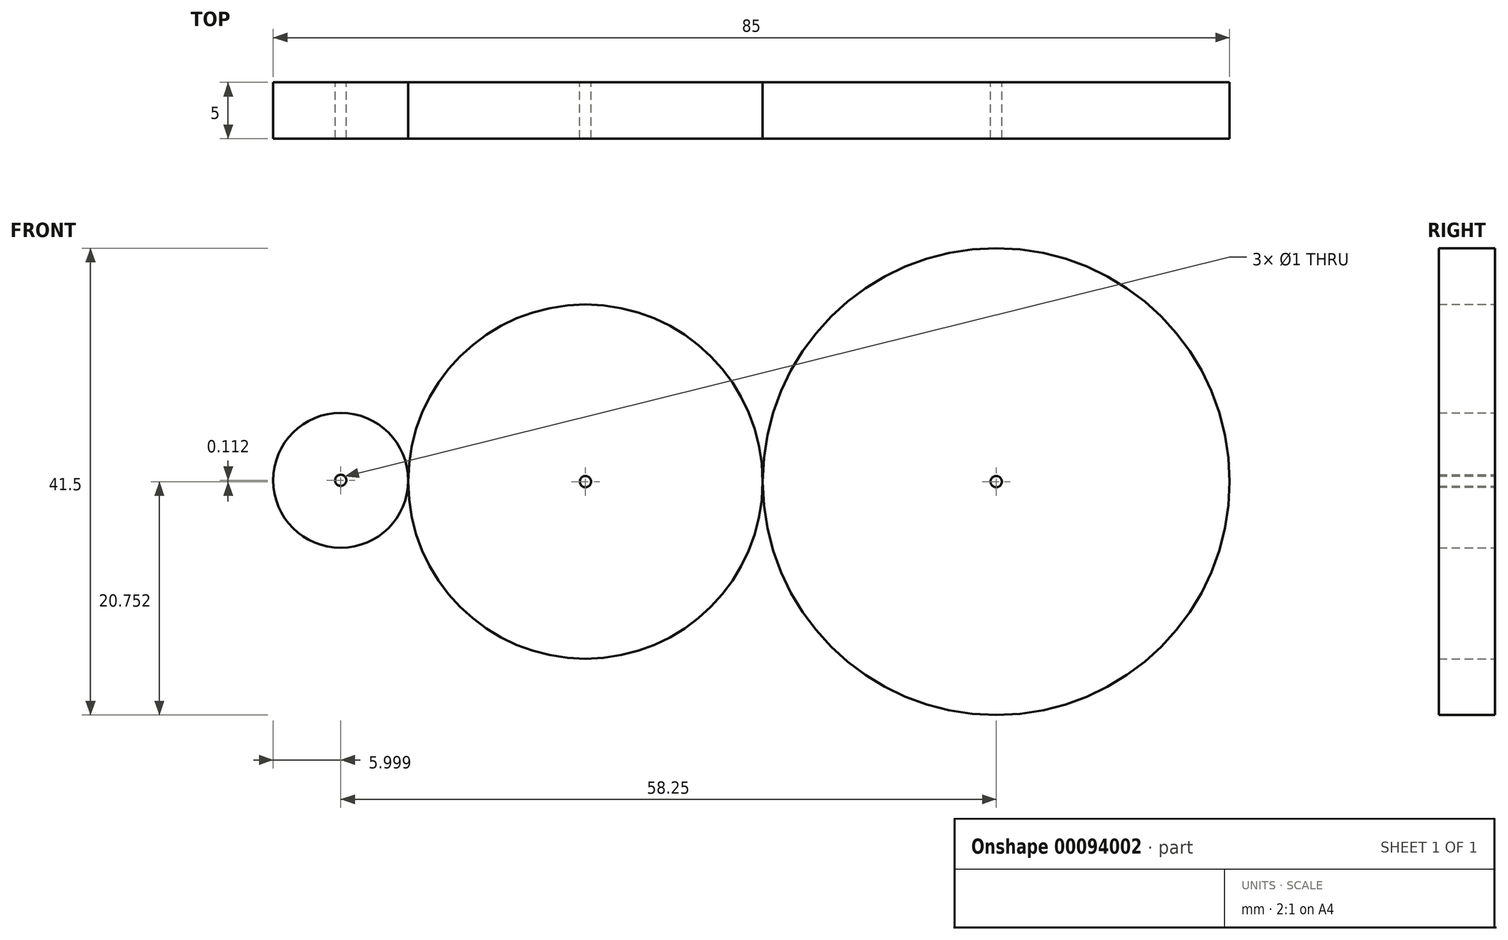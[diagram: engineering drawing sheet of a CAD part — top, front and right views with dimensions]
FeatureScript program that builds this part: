
annotation { "Feature Type Name" : "Feature", "Feature Type Description" : "" }
export const myFeature = defineFeature(function(context is Context, id is Id, definition is map)
    precondition{}
    {
        {
            var Q0;
            Q0=qCreatedBy(makeId("Front.planeOp"),FACE);
            var sketch = newSketch(context, id + "F0", { "sketchPlane" : qUnion([Q0])});
            skCircle(sketch, "E0", {"center": v(-29.78, 0.26) * mm, "radius": 6 * mm});
            skCircle(sketch, "E1", {"center": v(-8.03, 0.15) * mm, "radius": 15.75 * mm});
            skCircle(sketch, "E2", {"center": v(28.47, 0.15) * mm, "radius": 20.75 * mm});
            skLineSegment(sketch, "E3.bottom", {"start": v(-58.84, 39.47) * mm, "end": v(64.34, 39.47) * mm});
            skLineSegment(sketch, "E3.top", {"start": v(-58.84, -32.96) * mm, "end": v(64.34, -32.96) * mm});
            skLineSegment(sketch, "E3.left", {"start": v(-58.84, 39.47) * mm, "end": v(-58.84, -32.96) * mm});
            skLineSegment(sketch, "E3.right", {"start": v(64.34, 39.47) * mm, "end": v(64.34, -32.96) * mm});
            skCircle(sketch, "E4", {"center": v(-29.78, 0.26) * mm, "radius": 0.5 * mm});
            skCircle(sketch, "E5", {"center": v(-8.03, 0.15) * mm, "radius": 0.5 * mm});
            skCircle(sketch, "E6", {"center": v(28.47, 0.15) * mm, "radius": 0.5 * mm});
            skSolve(sketch);
        }
        {
            var Q0;
            Q0=makeQuery(id+"F0.imprint","IMPRINT",FACE,{"disambiguationData":[TD([[makeQuery(id+"F0.imprint","IMPRINT",EDGE,{"derivedFrom":sQuery(id+"F0.wireOp",EDGE,"E0")}),1.0]])]});
            extrude(context, id + "F1", {"entities" : qUnion([Q0]), "depth" : 5 * mm});
        }
        {
            var Q0;
            {var subQ0=sQuery(id+"F0.wireOp",EDGE,"E1");var subQ1=makeQuery(id+"F0.imprint","INTERSECT",VERTEX,{"derivedFrom":[sQuery(id+"F0.wireOp",EDGE,"E0"),subQ0]});Q0=makeQuery(id+"F0.imprint","IMPRINT",FACE,{"disambiguationData":[TD([[makeQuery(id+"F0.imprint","IMPRINT",EDGE,{"disambiguationData":[TD([[subQ1,1.0]])],"derivedFrom":subQ0}),1.0]])]});}
            extrude(context, id + "F2", {"entities" : qUnion([Q0]), "operationType" : NewBodyOperationType.ADD, "depth" : 5 * mm});
        }
        {
            var Q0;
            Q0=makeQuery(id+"F0.imprint","IMPRINT",FACE,{"disambiguationData":[TD([[makeQuery(id+"F0.imprint","IMPRINT",EDGE,{"derivedFrom":sQuery(id+"F0.wireOp",EDGE,"E2")}),1.0]])]});
            extrude(context, id + "F3", {"entities" : qUnion([Q0]), "operationType" : NewBodyOperationType.ADD, "depth" : 5 * mm});
        }
    });
